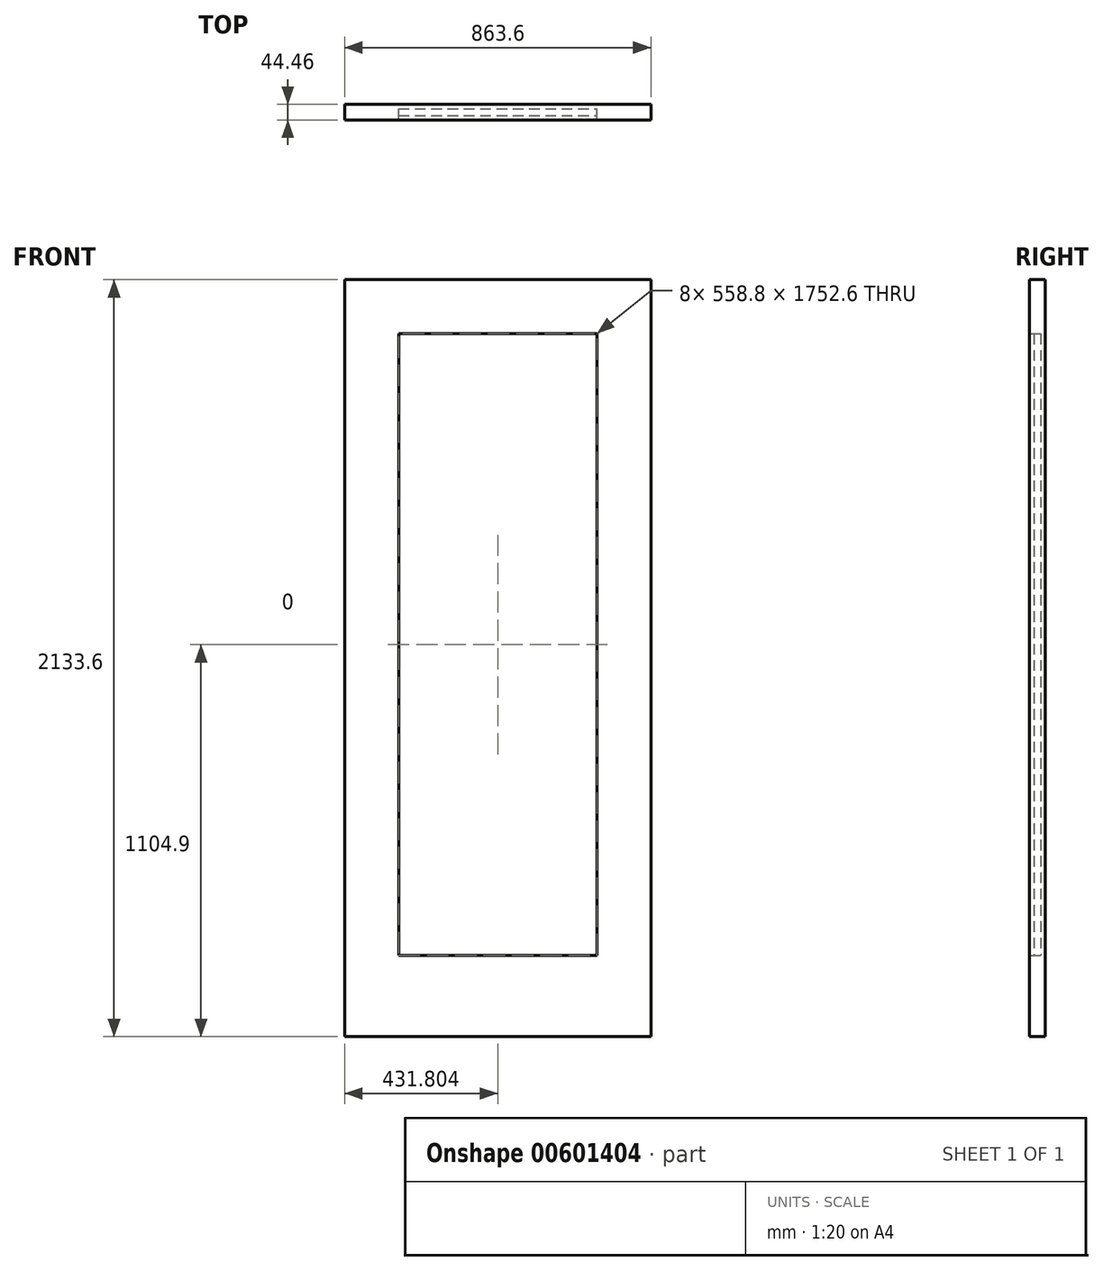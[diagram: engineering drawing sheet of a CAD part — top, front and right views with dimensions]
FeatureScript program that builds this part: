
annotation { "Feature Type Name" : "Feature", "Feature Type Description" : "" }
export const myFeature = defineFeature(function(context is Context, id is Id, definition is map)
    precondition{}
    {
        {
            var Q0;
            Q0=qCreatedBy(makeId("Front.planeOp"),FACE);
            var sketch = newSketch(context, id + "F0", { "sketchPlane" : qUnion([Q0])});
            skLineSegment(sketch, "E0.bottom", {"start": v(96.02, 1956.38) * mm, "end": v(959.62, 1956.38) * mm});
            skLineSegment(sketch, "E0.top", {"start": v(96.02, -177.22) * mm, "end": v(959.62, -177.22) * mm});
            skLineSegment(sketch, "E0.left", {"start": v(96.02, 1956.38) * mm, "end": v(96.02, -177.22) * mm});
            skLineSegment(sketch, "E0.right", {"start": v(959.62, 1956.38) * mm, "end": v(959.62, -177.22) * mm});
            skLineSegment(sketch, "E1.bottom", {"start": v(248.42, 1803.98) * mm, "end": v(807.22, 1803.98) * mm});
            skLineSegment(sketch, "E1.top", {"start": v(248.42, 51.38) * mm, "end": v(807.22, 51.38) * mm});
            skLineSegment(sketch, "E1.left", {"start": v(248.42, 1803.98) * mm, "end": v(248.42, 51.38) * mm});
            skLineSegment(sketch, "E1.right", {"start": v(807.22, 1803.98) * mm, "end": v(807.22, 51.38) * mm});
            skSolve(sketch);
        }
        {
            var Q0;
            Q0=makeQuery(id+"F0.imprint","IMPRINT",FACE,{"disambiguationData":[TD([[makeQuery(id+"F0.imprint","IMPRINT",EDGE,{"derivedFrom":sQuery(id+"F0.wireOp",EDGE,"E0.bottom")}),-1.0]])]});
            extrude(context, id + "F1", {"entities" : qUnion([Q0]), "endBound" : BoundingType.SYMMETRIC, "depth" : 44.45 * mm, "offsetDistance" : 25.4 * mm});
        }
        {
            var Q0;
            {var subQ16=sQuery(id+"F0.wireOp",EDGE,"E1.bottom");Q0=makeQuery(id+"F0.imprint","IMPRINT",FACE,{"disambiguationData":[TD([[makeQuery(id+"F0.imprint","IMPRINT",EDGE,{"derivedFrom":subQ16}),-1.0]])]});}
            extrude(context, id + "F2", {"entities" : qUnion([Q0]), "endBound" : BoundingType.SYMMETRIC, "depth" : 19.05 * mm, "offsetDistance" : 25.4 * mm});
        }
    });
